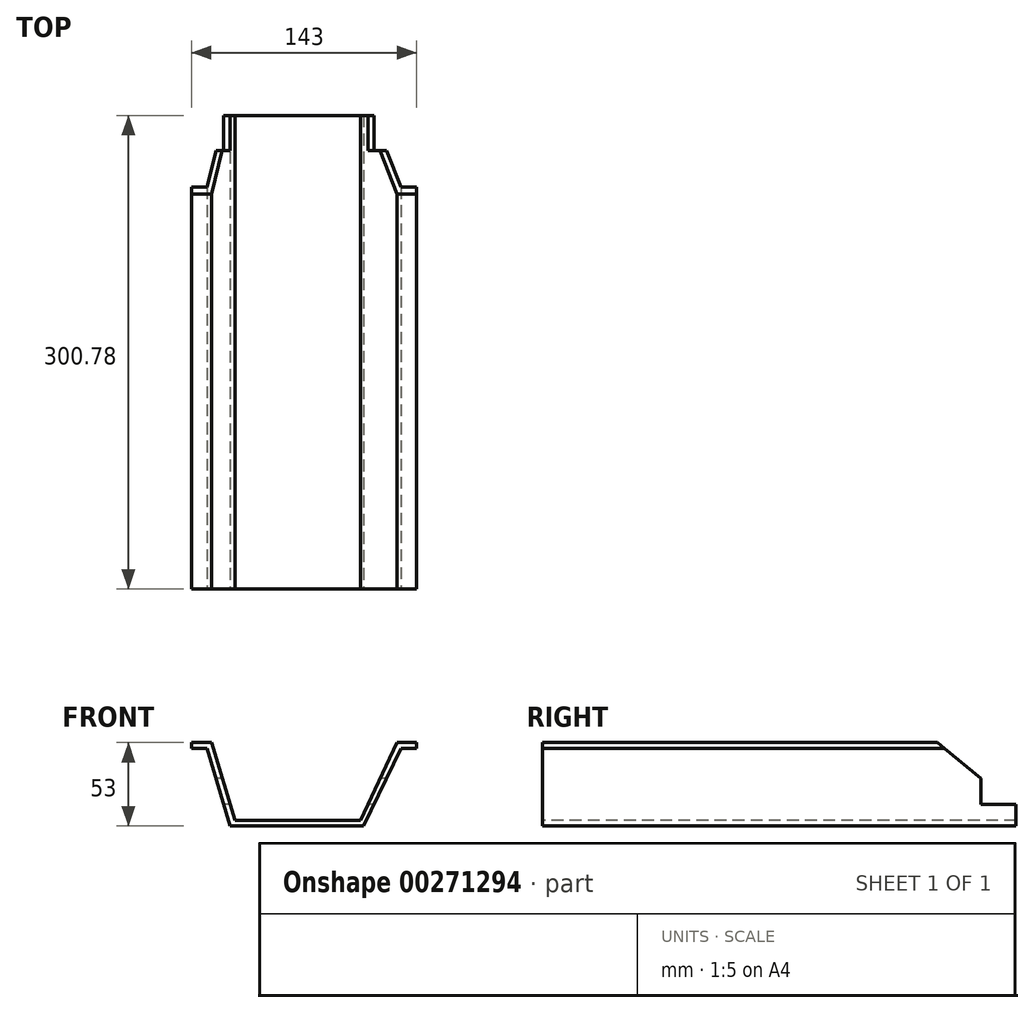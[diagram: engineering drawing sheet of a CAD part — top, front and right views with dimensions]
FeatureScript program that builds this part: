
annotation { "Feature Type Name" : "Feature", "Feature Type Description" : "" }
export const myFeature = defineFeature(function(context is Context, id is Id, definition is map)
    precondition{}
    {
        {
            var Q0;
            Q0=qCreatedBy(makeId("Front.planeOp"),FACE);
            var sketch = newSketch(context, id + "F0", { "sketchPlane" : qUnion([Q0])});
            skLineSegment(sketch, "E0.bottom", {"start": v(-67.68, 1.34) * mm, "end": v(75.32, 1.34) * mm});
            skLineSegment(sketch, "E0.top", {"start": v(-67.68, -51.66) * mm, "end": v(75.32, -51.66) * mm});
            skLineSegment(sketch, "E0.left", {"start": v(-67.68, 1.34) * mm, "end": v(-67.68, -51.66) * mm});
            skLineSegment(sketch, "E0.right", {"start": v(75.32, 1.34) * mm, "end": v(75.32, -51.66) * mm});
            skSolve(sketch);
        }
        {
            var Q0;
            Q0=makeQuery(id+"F0.imprint","IMPRINT",FACE,{"disambiguationData":[TD([[makeQuery(id+"F0.imprint","IMPRINT",EDGE,{"derivedFrom":sQuery(id+"F0.wireOp",EDGE,"E0.bottom")}),-1.0]])]});
            extrude(context, id + "F1", {"entities" : qUnion([Q0]), "depth" : 365 * mm});
        }
        {
            var Q0;
            Q0=makeQuery(id+"F1.opExtrude","SWEPT_FACE",FACE,{"disambiguationData":[OSD([sQuery(id+"F0.wireOp",EDGE,"E0.left")])]});
            var sketch = newSketch(context, id + "F2", { "sketchPlane" : qUnion([Q0])});
            skLineSegment(sketch, "E1", {"start": v(365, -51.66) * mm, "end": v(365, 1.34) * mm});
            skLineSegment(sketch, "E2", {"start": v(427.43, 1.34) * mm, "end": v(365, 1.34) * mm});
            skLineSegment(sketch, "E3", {"start": v(427.43, 1.34) * mm, "end": v(441.85, -51.66) * mm});
            skLineSegment(sketch, "E4", {"start": v(365, -51.66) * mm, "end": v(441.85, -51.66) * mm});
            skLineSegment(sketch, "E5", {"start": v(0, -25.16) * mm, "end": v(0, -16.49) * mm});
            skLineSegment(sketch, "E6", {"start": v(64.22, -51.66) * mm, "end": v(64.22, -37.96) * mm});
            skLineSegment(sketch, "E7", {"start": v(64.22, -37.96) * mm, "end": v(86.62, -37.96) * mm});
            skLineSegment(sketch, "E8", {"start": v(86.62, -37.96) * mm, "end": v(86.62, -21.31) * mm});
            skLineSegment(sketch, "E9", {"start": v(86.62, -21.31) * mm, "end": v(114.2, 1.34) * mm});
            skLineSegment(sketch, "E10", {"start": v(114.2, 1.34) * mm, "end": v(0, 1.34) * mm});
            skLineSegment(sketch, "E11", {"start": v(0, 1.34) * mm, "end": v(0, -16.49) * mm});
            skLineSegment(sketch, "E12", {"start": v(0, 1.34) * mm, "end": v(114.2, 1.34) * mm});
            skLineSegment(sketch, "E13", {"start": v(64.22, -51.66) * mm, "end": v(0, -51.66) * mm});
            skLineSegment(sketch, "E14", {"start": v(0, -51.66) * mm, "end": v(0, -25.16) * mm});
            skSolve(sketch);
        }
        {
            var Q0;
            Q0=makeQuery(id+"F2.imprint","IMPRINT",FACE,{"disambiguationData":[TD([[makeQuery(id+"F2.imprint","IMPRINT",EDGE,{"derivedFrom":sQuery(id+"F2.wireOp",EDGE,"E5")}),1.0]])]});
            extrude(context, id + "F3", {"entities" : qUnion([Q0]), "operationType" : NewBodyOperationType.REMOVE, "endBound" : BoundingType.THROUGH_ALL, "oppositeDirection" : true, "depth" : 25 * mm});
        }
        {
            var Q0;
            Q0=makeQuery(id+"F1.opExtrude","CAP_FACE",FACE,{"disambiguationData":[OSD([sQuery(id+"F0.wireOp",EDGE,"E0.bottom"),sQuery(id+"F0.wireOp",EDGE,"E0.top"),sQuery(id+"F0.wireOp",EDGE,"E0.left"),sQuery(id+"F0.wireOp",EDGE,"E0.right")])],"isStart":false});
            var sketch = newSketch(context, id + "F4", { "sketchPlane" : qUnion([Q0])});
            skLineSegment(sketch, "E15", {"start": v(-67.68, -2.32) * mm, "end": v(-57.7, -2.32) * mm});
            skLineSegment(sketch, "E16", {"start": v(-57.7, -2.32) * mm, "end": v(-43.21, -51.66) * mm});
            skLineSegment(sketch, "E17", {"start": v(-43.21, -51.66) * mm, "end": v(41.79, -51.66) * mm});
            skLineSegment(sketch, "E18", {"start": v(41.79, -51.66) * mm, "end": v(65.37, -2.32) * mm});
            skLineSegment(sketch, "E19", {"start": v(65.37, -2.32) * mm, "end": v(75.32, -2.32) * mm});
            skLineSegment(sketch, "E20", {"start": v(-67.68, -2.32) * mm, "end": v(-67.68, 1.34) * mm});
            skLineSegment(sketch, "E21", {"start": v(75.32, 1.34) * mm, "end": v(75.32, -2.32) * mm});
            skLineSegment(sketch, "E22", {"start": v(-67.68, 1.34) * mm, "end": v(-54.89, 1.34) * mm});
            skLineSegment(sketch, "E23", {"start": v(-54.89, 1.34) * mm, "end": v(-39.95, -48.1) * mm});
            skLineSegment(sketch, "E24", {"start": v(-39.95, -48.1) * mm, "end": v(39.71, -48.1) * mm});
            skLineSegment(sketch, "E25", {"start": v(39.71, -48.1) * mm, "end": v(62.93, 1.34) * mm});
            skSolve(sketch);
        }
        {
            var Q0;
            {var subQ0=sQuery(id+"F4.wireOp",EDGE,"E15");Q0=makeQuery(id+"F4.imprint","IMPRINT",FACE,{"disambiguationData":[TD([[makeQuery(id+"F4.imprint","IMPRINT",EDGE,{"derivedFrom":subQ0}),-1.0]])]});}
            var Q1;
            {var subQ0=sQuery(id+"F4.wireOp",EDGE,"E18");Q1=makeQuery(id+"F4.imprint","IMPRINT",FACE,{"disambiguationData":[TD([[makeQuery(id+"F4.imprint","IMPRINT",EDGE,{"derivedFrom":subQ0}),-1.0]])]});}
            extrude(context, id + "F5", {"entities" : qUnion([Q0, Q1]), "operationType" : NewBodyOperationType.REMOVE, "endBound" : BoundingType.THROUGH_ALL, "oppositeDirection" : true, "depth" : 25 * mm});
        }
        {
            var Q0;
            {var subQ0=sQuery(id+"F4.wireOp",EDGE,"E23");Q0=makeQuery(id+"F4.imprint","IMPRINT",FACE,{"disambiguationData":[TD([[makeQuery(id+"F4.imprint","IMPRINT",EDGE,{"derivedFrom":subQ0}),1.0]])]});}
            extrude(context, id + "F6", {"entities" : qUnion([Q0]), "operationType" : NewBodyOperationType.REMOVE, "endBound" : BoundingType.THROUGH_ALL, "oppositeDirection" : true, "depth" : 25 * mm});
        }
    });
